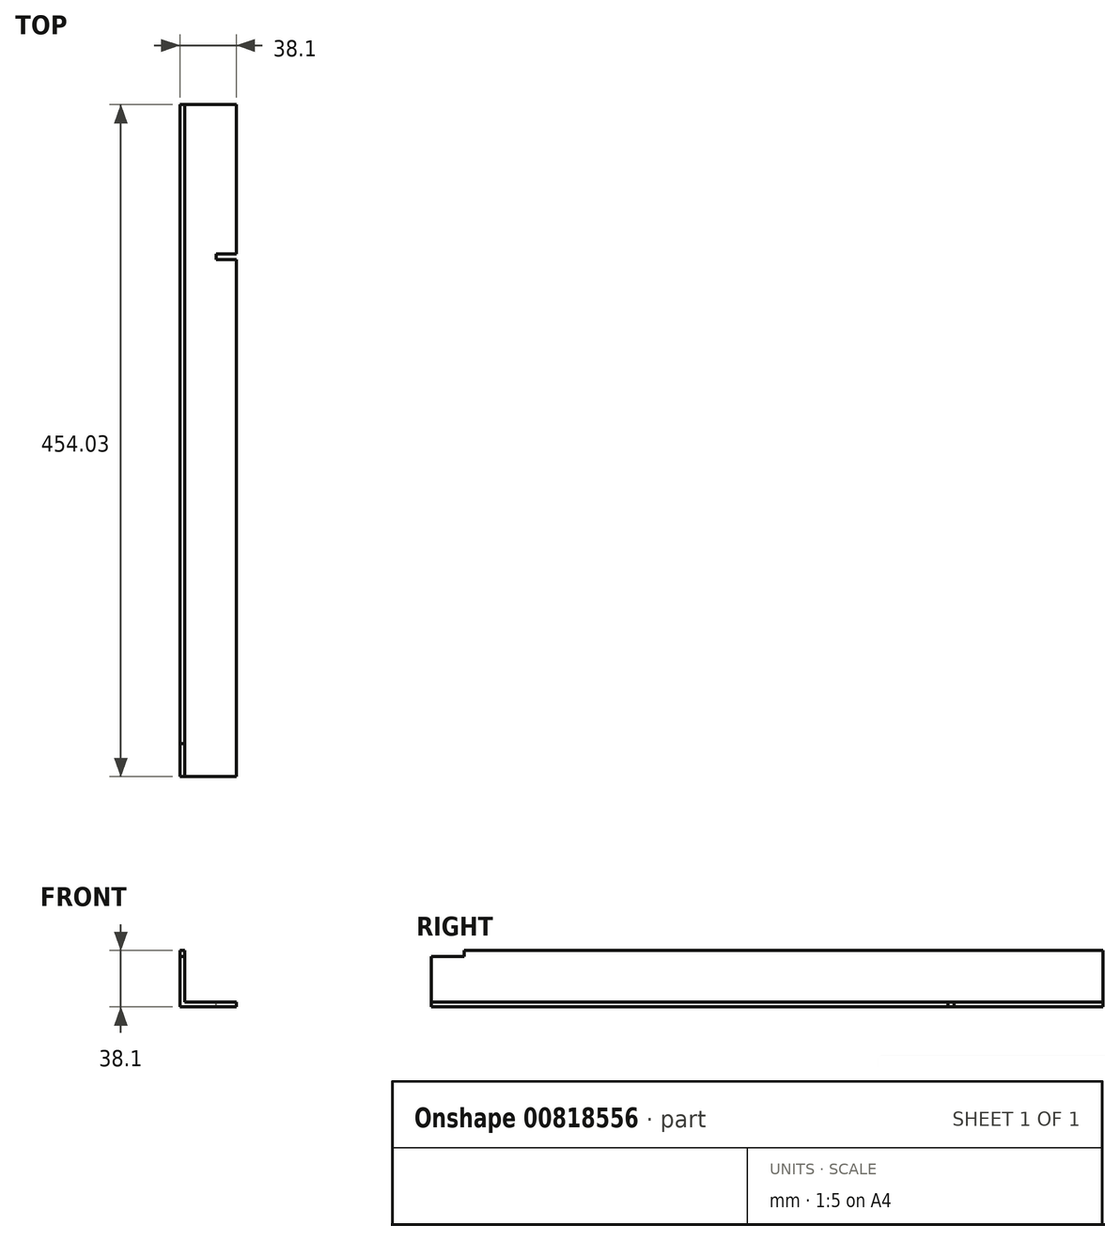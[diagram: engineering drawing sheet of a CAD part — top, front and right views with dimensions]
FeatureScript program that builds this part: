
annotation { "Feature Type Name" : "Feature", "Feature Type Description" : "" }
export const myFeature = defineFeature(function(context is Context, id is Id, definition is map)
    precondition{}
    {
        {
            var Q0;
            Q0=qCreatedBy(makeId("Front.planeOp"),FACE);
            var sketch = newSketch(context, id + "F0", { "sketchPlane" : qUnion([Q0])});
            skLineSegment(sketch, "E0", {"start": v(-21.73, 20.45) * mm, "end": v(-21.73, -17.65) * mm});
            skLineSegment(sketch, "E1", {"start": v(-21.73, -17.65) * mm, "end": v(16.37, -17.65) * mm});
            skLineSegment(sketch, "E2", {"start": v(16.37, -17.65) * mm, "end": v(16.37, -14.47) * mm});
            skLineSegment(sketch, "E3", {"start": v(16.37, -14.47) * mm, "end": v(-18.55, -14.47) * mm});
            skLineSegment(sketch, "E4", {"start": v(-18.55, -14.47) * mm, "end": v(-18.55, 20.45) * mm});
            skLineSegment(sketch, "E5", {"start": v(-18.55, 20.45) * mm, "end": v(-21.73, 20.45) * mm});
            skSolve(sketch);
        }
        {
            var Q0;
            Q0=makeQuery(id+"F0.imprint","IMPRINT",FACE,{"disambiguationData":[TD([[makeQuery(id+"F0.imprint","IMPRINT",EDGE,{"derivedFrom":sQuery(id+"F0.wireOp",EDGE,"E0")}),1.0]])]});
            extrude(context, id + "F1", {"entities" : qUnion([Q0]), "depth" : 454.02 * mm, "offsetDistance" : 25.4 * mm});
        }
        {
            var Q0;
            Q0=makeQuery(id+"F1.opExtrude","SWEPT_FACE",FACE,{"disambiguationData":[OSD([sQuery(id+"F0.wireOp",EDGE,"E1")])]});
            var sketch = newSketch(context, id + "F2", { "sketchPlane" : qUnion([Q0])});
            skLineSegment(sketch, "E6", {"start": v(16.37, 454.03) * mm, "end": v(12.4, 454.03) * mm});
            skLineSegment(sketch, "E7", {"start": v(12.4, 454.03) * mm, "end": v(12.4, 431.8) * mm});
            skLineSegment(sketch, "E8", {"start": v(12.4, 431.8) * mm, "end": v(16.37, 431.8) * mm});
            skLineSegment(sketch, "E9", {"start": v(16.37, 431.8) * mm, "end": v(16.37, 454.03) * mm});
            skSolve(sketch);
        }
        {
            var Q0;
            Q0=makeQuery(id+"F1.opExtrude","SWEPT_FACE",FACE,{"disambiguationData":[OSD([sQuery(id+"F0.wireOp",EDGE,"E0")])]});
            var sketch = newSketch(context, id + "F3", { "sketchPlane" : qUnion([Q0])});
            skLineSegment(sketch, "E10", {"start": v(454.03, 16.48) * mm, "end": v(454.03, 20.45) * mm});
            skLineSegment(sketch, "E11", {"start": v(454.03, 20.45) * mm, "end": v(431.8, 20.45) * mm});
            skLineSegment(sketch, "E12", {"start": v(431.8, 20.45) * mm, "end": v(431.8, 16.48) * mm});
            skLineSegment(sketch, "E13", {"start": v(431.8, 16.48) * mm, "end": v(454.03, 16.48) * mm});
            skSolve(sketch);
        }
        {
            var Q0;
            Q0 = qSketchRegion(id + "F3", true);
            extrude(context, id + "F4", {"entities" : qUnion([Q0]), "operationType" : NewBodyOperationType.REMOVE, "oppositeDirection" : true, "depth" : 25.4 * mm, "offsetDistance" : 25.4 * mm});
        }
        {
            var Q0;
            Q0=makeQuery(id+"F1.opExtrude","SWEPT_FACE",FACE,{"disambiguationData":[OSD([sQuery(id+"F0.wireOp",EDGE,"E3")])]});
            var sketch = newSketch(context, id + "F5", { "sketchPlane" : qUnion([Q0])});
            skLineSegment(sketch, "E14", {"start": v(16.37, -104.78) * mm, "end": v(2.88, -104.78) * mm});
            skLineSegment(sketch, "E15", {"start": v(2.88, -104.78) * mm, "end": v(2.88, -100.8) * mm});
            skLineSegment(sketch, "E16", {"start": v(2.88, -100.8) * mm, "end": v(16.37, -100.8) * mm});
            skLineSegment(sketch, "E17", {"start": v(16.37, -100.8) * mm, "end": v(16.37, -104.78) * mm});
            skSolve(sketch);
        }
        {
            var Q0;
            Q0 = qSketchRegion(id + "F5", true);
            extrude(context, id + "F6", {"entities" : qUnion([Q0]), "operationType" : NewBodyOperationType.REMOVE, "oppositeDirection" : true, "depth" : 25.4 * mm, "offsetDistance" : 25.4 * mm});
        }
    });
